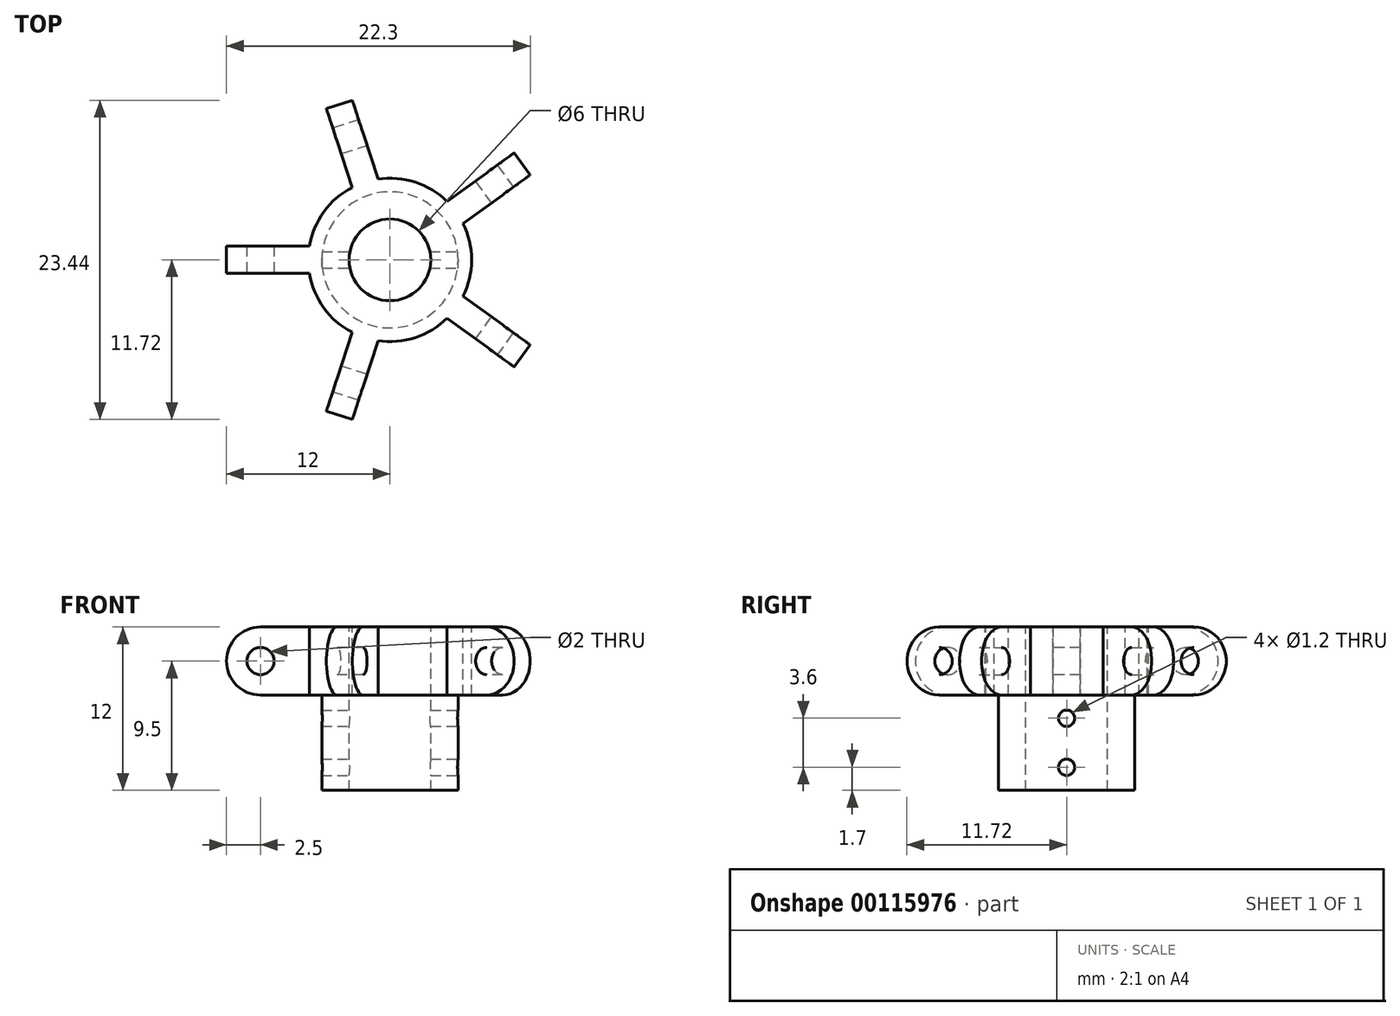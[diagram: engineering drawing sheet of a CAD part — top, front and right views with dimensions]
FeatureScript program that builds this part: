
annotation { "Feature Type Name" : "Feature", "Feature Type Description" : "" }
export const myFeature = defineFeature(function(context is Context, id is Id, definition is map)
    precondition{}
    {
        {
            var Q0;
            Q0=qCreatedBy(makeId("Front.planeOp"),FACE);
            var sketch = newSketch(context, id + "F0", { "sketchPlane" : qUnion([Q0])});
            skLineSegment(sketch, "E0", {"start": v(-3, 5) * mm, "end": v(-6, 5) * mm});
            skLineSegment(sketch, "E1", {"start": v(-6, 5) * mm, "end": v(-6, 0) * mm});
            skLineSegment(sketch, "E2", {"start": v(-6, 0) * mm, "end": v(-5, 0) * mm});
            skLineSegment(sketch, "E3", {"start": v(-5, 0) * mm, "end": v(-5, -7) * mm});
            skLineSegment(sketch, "E4", {"start": v(-5, -7) * mm, "end": v(-3, -7) * mm});
            skLineSegment(sketch, "E5", {"start": v(-3, -7) * mm, "end": v(-3, 5) * mm});
            skLineSegment(sketch, "E6", {"start": v(0, 11.9) * mm, "end": v(0, -21.79) * mm, "construction": true});
            skSolve(sketch);
        }
        {
            var Q0;
            Q0=qSketchRegion(id+"F0",true);
            var Q1;
            Q1=sQuery(id+"F0.wireOp",EDGE,"E6");
            revolve(context, id + "F1", {"entities" : qUnion([Q0]), "axis" : qUnion([Q1]), "revolveType" : RevolveType.FULL});
        }
        {
            var Q0;
            Q0=qCreatedBy(makeId("Front.planeOp"),FACE);
            var sketch = newSketch(context, id + "F2", { "sketchPlane" : qUnion([Q0])});
            skLineSegment(sketch, "E7", {"start": v(-9.5, 5) * mm, "end": v(-5, 5) * mm});
            skLineSegment(sketch, "E8", {"start": v(-5, 5) * mm, "end": v(-5, 0) * mm});
            skLineSegment(sketch, "E9", {"start": v(-5, 0) * mm, "end": v(-9.5, 0) * mm});
            skLineSegment(sketch, "E10", {"start": v(-9.5, 0) * mm, "end": v(-9.5, 5) * mm, "construction": true});
            skArc(sketch, "E11", {"start": v(-9.5, 5) * mm, "mid": v(-12, 2.5) * mm, "end": v(-9.5, 0) * mm});
            skCircle(sketch, "E12", {"center": v(-9.5, 2.5) * mm, "radius": 2.5 * mm});
            skSolve(sketch);
        }
        {
            var Q0;
            Q0=qSketchRegion(id+"F2",true);
            extrude(context, id + "F3", {"entities" : qUnion([Q0]), "endBound" : BoundingType.SYMMETRIC, "depth" : 2 * mm});
        }
        {
            var Q0;
            Q0=makeQuery(id+"F3.opExtrude","CAP_FACE",FACE,{"disambiguationData":[OSD([sQuery(id+"F2.wireOp",EDGE,"E7"),sQuery(id+"F2.wireOp",EDGE,"E8"),sQuery(id+"F2.wireOp",EDGE,"E9"),sQuery(id+"F2.wireOp",EDGE,"E12")])],"isStart":false});
            var sketch = newSketch(context, id + "F4", { "sketchPlane" : qUnion([Q0])});
            skCircle(sketch, "E13", {"center": v(-9.5, 2.5) * mm, "radius": 1 * mm});
            skSolve(sketch);
        }
        {
            var Q0;
            Q0=makeQuery(id+"F4.imprint","IMPRINT",FACE,{"disambiguationData":[TD([[makeQuery(id+"F4.imprint","IMPRINT",EDGE,{"derivedFrom":sQuery(id+"F4.wireOp",EDGE,"E13")}),1.0]])]});
            extrude(context, id + "F5", {"entities" : qUnion([Q0]), "operationType" : NewBodyOperationType.REMOVE, "endBound" : BoundingType.THROUGH_ALL, "oppositeDirection" : true, "depth" : 25 * mm});
        }
        {
            var Q0;
            Q0=makeQuery(id+"F3.opExtrude","SWEPT_BODY",BODY,{"disambiguationData":[OSD([sQuery(id+"F2.wireOp",EDGE,"E7"),sQuery(id+"F2.wireOp",EDGE,"E8"),sQuery(id+"F2.wireOp",EDGE,"E9"),sQuery(id+"F2.wireOp",EDGE,"E11"),sQuery(id+"F2.wireOp",EDGE,"E12")])]});
            var Q1;
            Q1=makeQuery(id+"F1.opRevolve","SWEPT_FACE",FACE,{"disambiguationData":[OSD([sQuery(id+"F0.wireOp",EDGE,"E5")])]});
            circularPattern(context, id + "F6", {"operationType" : NewBodyOperationType.ADD, "entities" : qUnion([Q0]), "axis" : qUnion([Q1]), "angle" : 360 * degree, "instanceCount" : 5, "equalSpace" : true});
        }
        {
            var Q0;
            Q0=qCreatedBy(makeId("Right.planeOp"),FACE);
            var sketch = newSketch(context, id + "F7", { "sketchPlane" : qUnion([Q0])});
            skCircle(sketch, "E14", {"center": v(0, -1.7) * mm, "radius": 0.6 * mm});
            skCircle(sketch, "E15", {"center": v(0, -5.3) * mm, "radius": 0.6 * mm});
            skLineSegment(sketch, "E16", {"start": v(0, -5.3) * mm, "end": v(0, -7) * mm, "construction": true});
            skLineSegment(sketch, "E17", {"start": v(0, -1.7) * mm, "end": v(0, 0) * mm, "construction": true});
            skSolve(sketch);
        }
        {
            var Q0;
            Q0=qSketchRegion(id+"F7",true);
            extrude(context, id + "F8", {"entities" : qUnion([Q0]), "operationType" : NewBodyOperationType.REMOVE, "endBound" : BoundingType.THROUGH_ALL, "oppositeDirection" : true, "depth" : 25 * mm, "hasSecondDirection" : true, "secondDirectionBound" : SecondDirectionBoundingType.THROUGH_ALL, "secondDirectionOppositeDirection" : false, "secondDirectionDepth" : 25 * mm});
        }
    });
